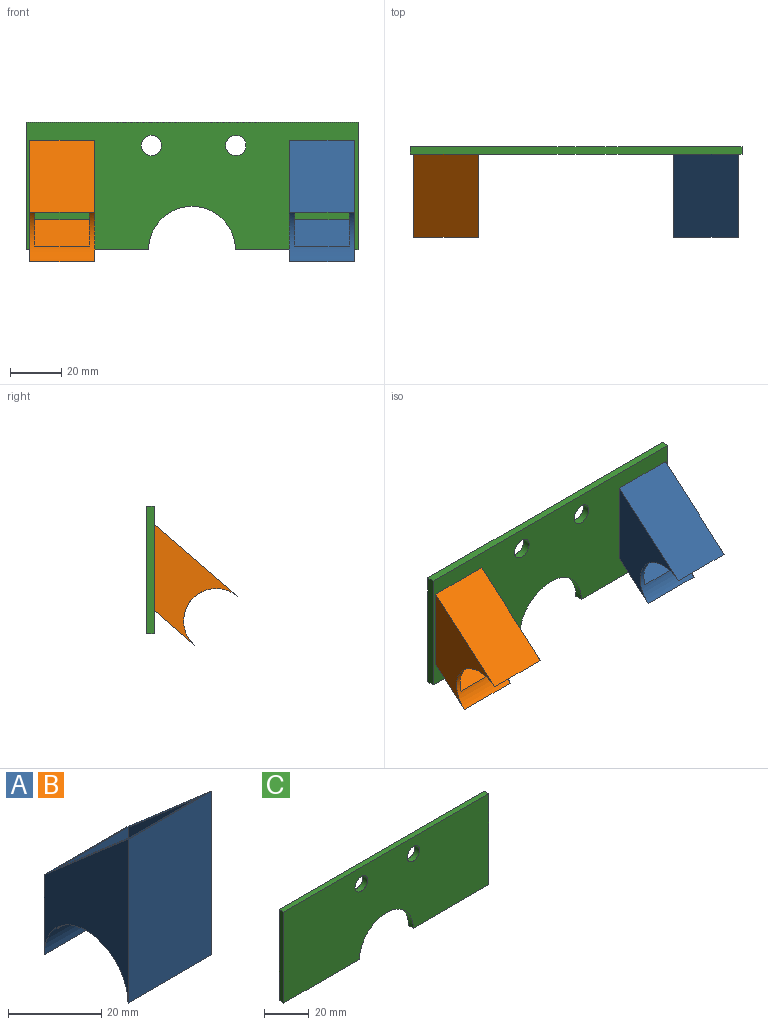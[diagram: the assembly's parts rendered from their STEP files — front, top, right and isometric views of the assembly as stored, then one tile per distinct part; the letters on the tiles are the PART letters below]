
ASSEMBLY  parts=3 mates=2
PART A: 10 faces, bbox 25.4x25.4x43 mm
  f0: plane 25.4x25.4mm, normal (0,0.65,0.76), area 247.7mm2, adj f1,f2,f3,f4,f5,f6,f7,f8
  f1: plane 43x25.4mm, normal (0,-1,0), area 1092.2mm2, adj f0,f3,f4,f9
  f2: plane 25.4x21mm, normal (0,1,0), area 533.4mm2, adj f0,f3,f4,f9
  f3: plane 43x25.4mm, normal (1,0,0), area 559.4mm2, adj f0,f1,f2,f9
  f4: plane 43x25.4mm, normal (-1,0,0), area 559.4mm2, adj f0,f1,f2,f9
  f5: plane 34.43x21.4mm, normal (0,1,0), area 736.7mm2, adj f0,f7,f8,f9
  f6: plane 21.4x15.89mm, normal (0,-1,0), area 340.1mm2, adj f0,f7,f8,f9
  f7: plane 34.43x21.4mm, normal (-1,0,0), area 450mm2, adj f0,f5,f6,f9
  f8: plane 34.43x21.4mm, normal (1,0,0), area 450mm2, adj f0,f5,f6,f9
  f9: cylinder r=12.7mm len=25.4mm, axis (1,0,0), area 468.8mm2, adj f1,f2,f3,f4,f5,f6,f7,f8
PART B: same geometry as A
PART C: 10 faces, bbox 129.8x3x49.8 mm
  f0: cylinder r=17mm len=34mm, axis (0,1,0), area 160.2mm2, adj f1,f7,f8,f9
  f1: plane 47.9x3mm, normal (0,0,-1), area 143.7mm2, adj f0,f2,f8,f9
  f2: plane 49.78x3mm, normal (1,0,0), area 149.4mm2, adj f1,f3,f8,f9
  f3: plane 129.79x3mm, normal (0,0,1), area 389.4mm2, adj f2,f4,f8,f9
  f4: plane 49.78x3mm, normal (-1,0,0), area 149.4mm2, adj f3,f7,f8,f9
  f5: cylinder r=4mm len=8mm, axis (0,1,0), area 75.4mm2, adj f8,f9
  f6: cylinder r=4mm len=8mm, axis (0,1,0), area 75.4mm2, adj f8,f9
  f7: plane 47.9x3mm, normal (0,0,-1), area 143.7mm2, adj f0,f4,f8,f9
  f8: plane 129.79x49.78mm, normal (0,-1,0), area 5907.2mm2, adj f0,f1,f2,f3,f4,f5,f6,f7
  f9: plane 129.79x49.78mm, normal (0,1,0), area 5907.2mm2, adj f0,f1,f2,f3,f4,f5,f6,f7
PLACE A rot(axis=(-1,0,0),49.1deg) t=(31.14,-15.17,2.64)mm
PLACE B rot(axis=(-1,0,0),49.1deg) t=(-70.46,-15.17,2.64)mm
PLACE C t=(-19.65,-5.73,8.42)mm
MATE fastened A.f0 <-> C.f8  axis (0,1,0) through (31.14,-7.23,9.51)mm
MATE fastened B.f0 <-> C.f8  axis (0,1,0) through (-70.46,-7.23,9.51)mm
